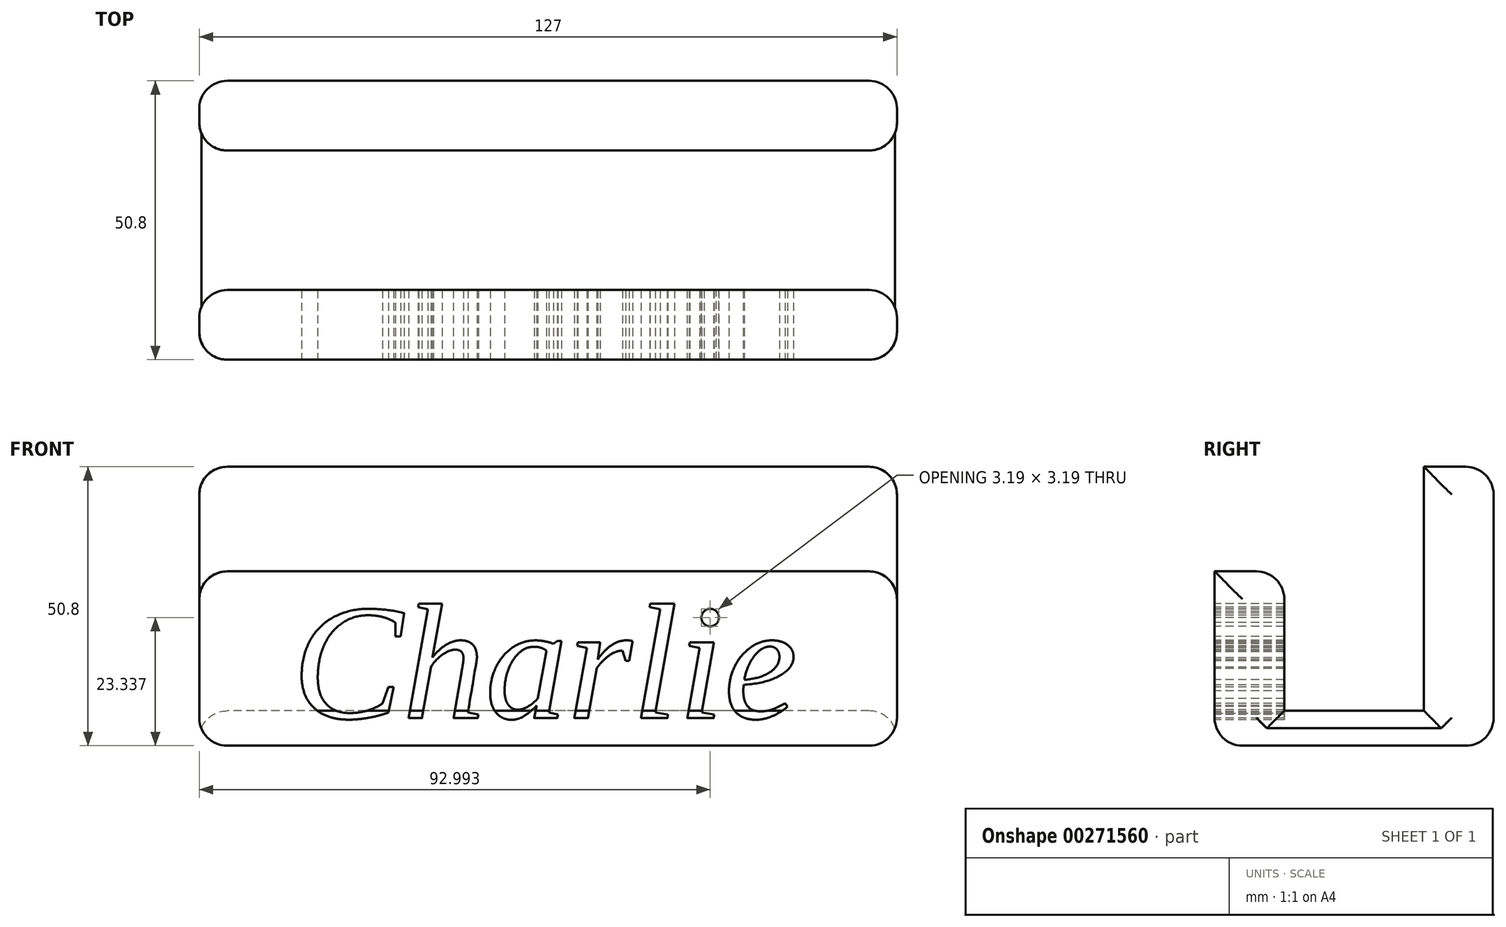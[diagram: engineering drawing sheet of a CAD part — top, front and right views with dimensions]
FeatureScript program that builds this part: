
annotation { "Feature Type Name" : "Feature", "Feature Type Description" : "" }
export const myFeature = defineFeature(function(context is Context, id is Id, definition is map)
    precondition{}
    {
        {
            var Q0;
            Q0=qCreatedBy(makeId("Front.planeOp"),FACE);
            var sketch = newSketch(context, id + "F0", { "sketchPlane" : qUnion([Q0])});
            skLineSegment(sketch, "E0.bottom", {"start": v(0, 0) * mm, "end": v(127, 0) * mm});
            skLineSegment(sketch, "E0.top", {"start": v(0, 50.8) * mm, "end": v(127, 50.8) * mm});
            skLineSegment(sketch, "E0.left", {"start": v(0, 0) * mm, "end": v(0, 50.8) * mm});
            skLineSegment(sketch, "E0.right", {"start": v(127, 0) * mm, "end": v(127, 50.8) * mm});
            skSolve(sketch);
        }
        {
            var Q0;
            Q0=makeQuery(id+"F0.imprint","IMPRINT",FACE,{"disambiguationData":[TD([[makeQuery(id+"F0.imprint","IMPRINT",EDGE,{"derivedFrom":sQuery(id+"F0.wireOp",EDGE,"E0.bottom")}),1.0]])]});
            extrude(context, id + "F1", {"entities" : qUnion([Q0]), "depth" : 50.8 * mm});
        }
        {
            var Q0;
            Q0=makeQuery(id+"F1.opExtrude","SWEPT_FACE",FACE,{"disambiguationData":[OSD([sQuery(id+"F0.wireOp",EDGE,"E0.left")])]});
            var sketch = newSketch(context, id + "F2", { "sketchPlane" : qUnion([Q0])});
            skLineSegment(sketch, "E1", {"start": v(0, 50.8) * mm, "end": v(12.7, 50.8) * mm});
            skLineSegment(sketch, "E2", {"start": v(12.7, 50.8) * mm, "end": v(12.7, 6.35) * mm});
            skLineSegment(sketch, "E3", {"start": v(12.7, 6.35) * mm, "end": v(38.1, 6.35) * mm});
            skLineSegment(sketch, "E4", {"start": v(38.1, 6.35) * mm, "end": v(38.1, 31.75) * mm});
            skLineSegment(sketch, "E5", {"start": v(38.1, 31.75) * mm, "end": v(50.8, 31.75) * mm});
            skSolve(sketch);
        }
        {
            var Q0;
            {var subQ5=sQuery(id+"F2.wireOp",EDGE,"E2");Q0=makeQuery(id+"F2.imprint","IMPRINT",FACE,{"disambiguationData":[TD([[makeQuery(id+"F2.imprint","IMPRINT",EDGE,{"derivedFrom":subQ5}),1.0]])]});}
            extrude(context, id + "F3", {"entities" : qUnion([Q0]), "operationType" : NewBodyOperationType.REMOVE, "endBound" : BoundingType.THROUGH_ALL, "oppositeDirection" : true, "depth" : 25.4 * mm});
        }
        {
            var Q0;
            Q0=makeQuery(id+"F3.boolean.opBoolean","COPY",EDGE,{"derivedFrom":makeQuery(id+"F3.opExtrude","SWEPT_EDGE",EDGE,{"disambiguationData":[OSD([sQuery(id+"F0.wireOp",EDGE,"E0.left"),sQuery(id+"F2.wireOp",EDGE,"E5")])]})});
            var Q1;
            Q1=makeQuery(id+"F3.boolean.opBoolean","COPY",EDGE,{"derivedFrom":makeQuery(id+"F3.opExtrude","CAP_EDGE",EDGE,{"disambiguationData":[OSD([sQuery(id+"F2.wireOp",EDGE,"E5")])],"isStart":true})});
            var Q2;
            Q2=makeQuery(id+"F3.boolean.opBoolean","INTERSECT",EDGE,{"derivedFrom":[makeQuery(id+"F1.opExtrude","SWEPT_FACE",FACE,{"disambiguationData":[OSD([sQuery(id+"F0.wireOp",EDGE,"E0.right")])]}),makeQuery(id+"F3.opExtrude","SWEPT_FACE",FACE,{"disambiguationData":[OSD([sQuery(id+"F2.wireOp",EDGE,"E5")])]})]});
            var Q3;
            Q3=makeQuery(id+"F3.boolean.opBoolean","COPY",EDGE,{"derivedFrom":makeQuery(id+"F3.opExtrude","SWEPT_EDGE",EDGE,{"disambiguationData":[OSD([sQuery(id+"F0.wireOp",EDGE,"E0.top"),sQuery(id+"F0.wireOp",EDGE,"E0.left"),sQuery(id+"F2.wireOp",EDGE,"E1"),sQuery(id+"F2.wireOp",EDGE,"E2")])]})});
            var Q4;
            Q4=makeQuery(id+"F1.opExtrude","SWEPT_EDGE",EDGE,{"disambiguationData":[OSD([sQuery(id+"F0.wireOp",EDGE,"E0.top"),sQuery(id+"F0.wireOp",EDGE,"E0.left")])]});
            var Q5;
            Q5=makeQuery(id+"F1.opExtrude","CAP_EDGE",EDGE,{"disambiguationData":[OSD([sQuery(id+"F0.wireOp",EDGE,"E0.top")])],"isStart":true});
            var Q6;
            Q6=makeQuery(id+"F1.opExtrude","SWEPT_EDGE",EDGE,{"disambiguationData":[OSD([sQuery(id+"F0.wireOp",EDGE,"E0.top"),sQuery(id+"F0.wireOp",EDGE,"E0.right")])]});
            var Q7;
            Q7=makeQuery(id+"F3.boolean.opBoolean","COPY",EDGE,{"derivedFrom":makeQuery(id+"F3.opExtrude","SWEPT_EDGE",EDGE,{"disambiguationData":[OSD([sQuery(id+"F2.wireOp",EDGE,"E4"),sQuery(id+"F2.wireOp",EDGE,"E5")])]})});
            var Q8;
            Q8=makeQuery(id+"F1.opExtrude","SWEPT_FACE",FACE,{"disambiguationData":[OSD([sQuery(id+"F0.wireOp",EDGE,"E0.left")])]});
            var Q9;
            Q9=makeQuery(id+"F1.opExtrude","SWEPT_FACE",FACE,{"disambiguationData":[OSD([sQuery(id+"F0.wireOp",EDGE,"E0.right")])]});
            var Q10;
            Q10=makeQuery(id+"F1.opExtrude","SWEPT_FACE",FACE,{"disambiguationData":[OSD([sQuery(id+"F0.wireOp",EDGE,"E0.bottom")])]});
            fillet(context, id + "F4", {"entities" : qUnion([Q0, Q1, Q2, Q3, Q4, Q5, Q6, Q7, Q8, Q9, Q10]), "radius" : 5.08 * mm, "tangentPropagation" : true, "allowEdgeOverflow" : false});
        }
        {
            var Q0;
            Q0=makeQuery(id+"F1.opExtrude","CAP_FACE",FACE,{"disambiguationData":[OSD([sQuery(id+"F0.wireOp",EDGE,"E0.bottom"),sQuery(id+"F0.wireOp",EDGE,"E0.top"),sQuery(id+"F0.wireOp",EDGE,"E0.left"),sQuery(id+"F0.wireOp",EDGE,"E0.right")])],"isStart":false});
            var sketch = newSketch(context, id + "F5", { "sketchPlane" : qUnion([Q0])});
            skPoint(sketch, "E6", {"position": v(17.08, 26.67) * mm});
            skPoint(sketch, "E7", {"position": v(109.92, 5.08) * mm});
            skText(sketch, "E8", { "text": "Charlie", "fontName": "Tinos-Italic.ttf"});
            const initialGuessF5  = {"E8": [0.01696, 0.00502, 1, 0, 0.02165]};
            skSetInitialGuess(sketch, initialGuessF5);
            skSolve(sketch);
        }
        {
            var Q0;
            Q0 = qSketchRegion(id + "F5", true);
            var Q1;
            Q1=makeQuery(id+"F3.boolean.opBoolean","COPY",FACE,{"derivedFrom":makeQuery(id+"F3.opExtrude","SWEPT_FACE",FACE,{"disambiguationData":[OSD([sQuery(id+"F2.wireOp",EDGE,"E4")])]})});
            extrude(context, id + "F6", {"entities" : qUnion([Q0]), "operationType" : NewBodyOperationType.REMOVE, "endBound" : BoundingType.UP_TO_SURFACE, "oppositeDirection" : true, "endBoundEntityFace" : qUnion([Q1]), "depth" : 25.4 * mm});
        }
    });
